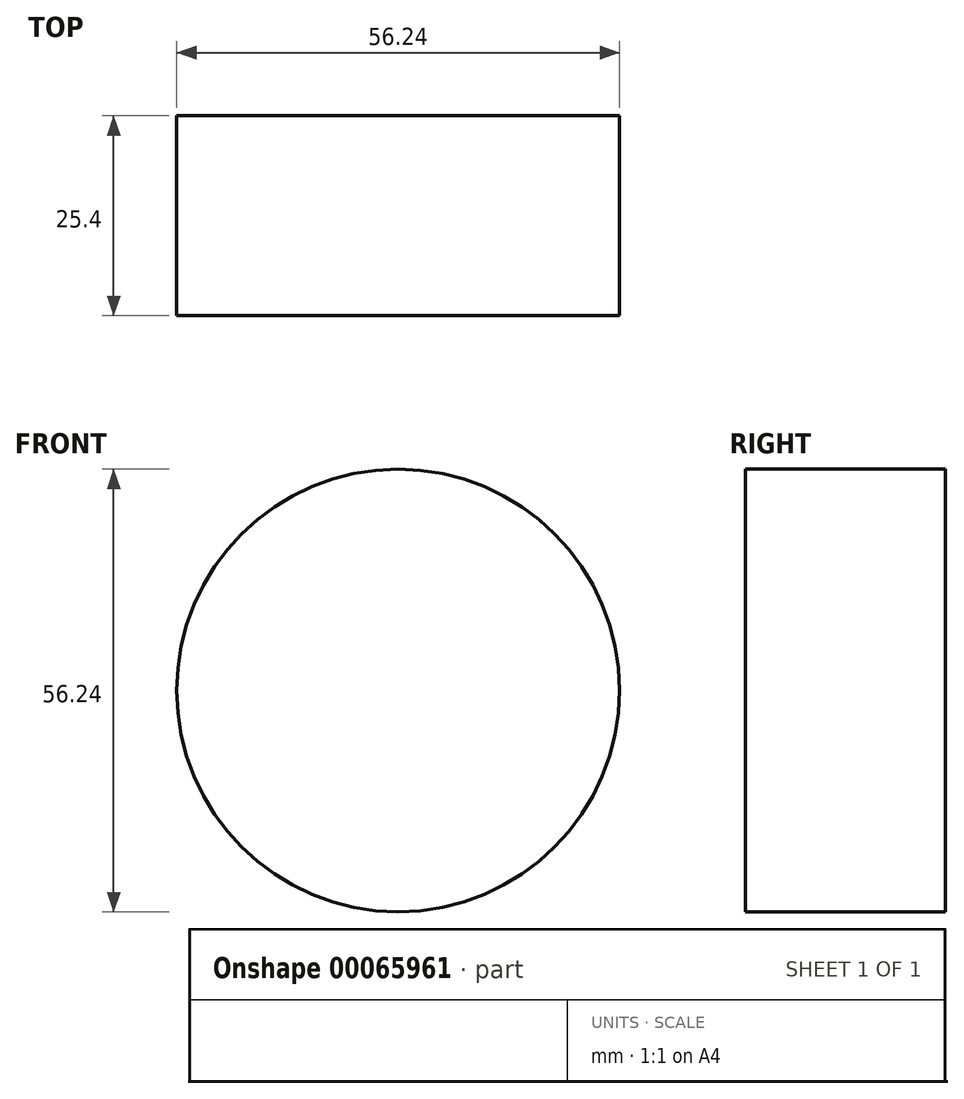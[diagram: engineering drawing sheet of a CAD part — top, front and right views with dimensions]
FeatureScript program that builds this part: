
annotation { "Feature Type Name" : "Feature", "Feature Type Description" : "" }
export const myFeature = defineFeature(function(context is Context, id is Id, definition is map)
    precondition{}
    {
        {
            var Q0;
            Q0=qCreatedBy(makeId("Front.planeOp"),FACE);
            var sketch = newSketch(context, id + "F0", { "sketchPlane" : qUnion([Q0])});
            skCircle(sketch, "E0", {"center": v(0, 0) * mm, "radius": 28.12 * mm});
            skSolve(sketch);
        }
        {
            var Q0;
            Q0=makeQuery(id+"F0.imprint","IMPRINT",FACE,{"disambiguationData":[TD([[makeQuery(id+"F0.imprint","IMPRINT",EDGE,{"derivedFrom":sQuery(id+"F0.wireOp",EDGE,"E0")}),1.0]])]});
            extrude(context, id + "F1", {"entities" : qUnion([Q0]), "depth" : 25.4 * mm});
        }
        {
            var Q0;
            Q0=qCreatedBy(makeId("Front.planeOp"),FACE);
            var sketch = newSketch(context, id + "F2", { "sketchPlane" : qUnion([Q0])});
            skCircle(sketch, "E1", {"center": v(0, 0) * mm, "radius": 13.44 * mm});
            skSolve(sketch);
        }
        {
            var Q0;
            Q0=sQuery(id+"F2.wireOp",EDGE,"E1");
            extrude(context, id + "F3", {"bodyType" : ToolBodyType.SURFACE, "surfaceEntities" : qUnion([Q0]), "endBound" : BoundingType.THROUGH_ALL, "oppositeDirection" : true, "depth" : 25.4 * mm});
        }
    });
